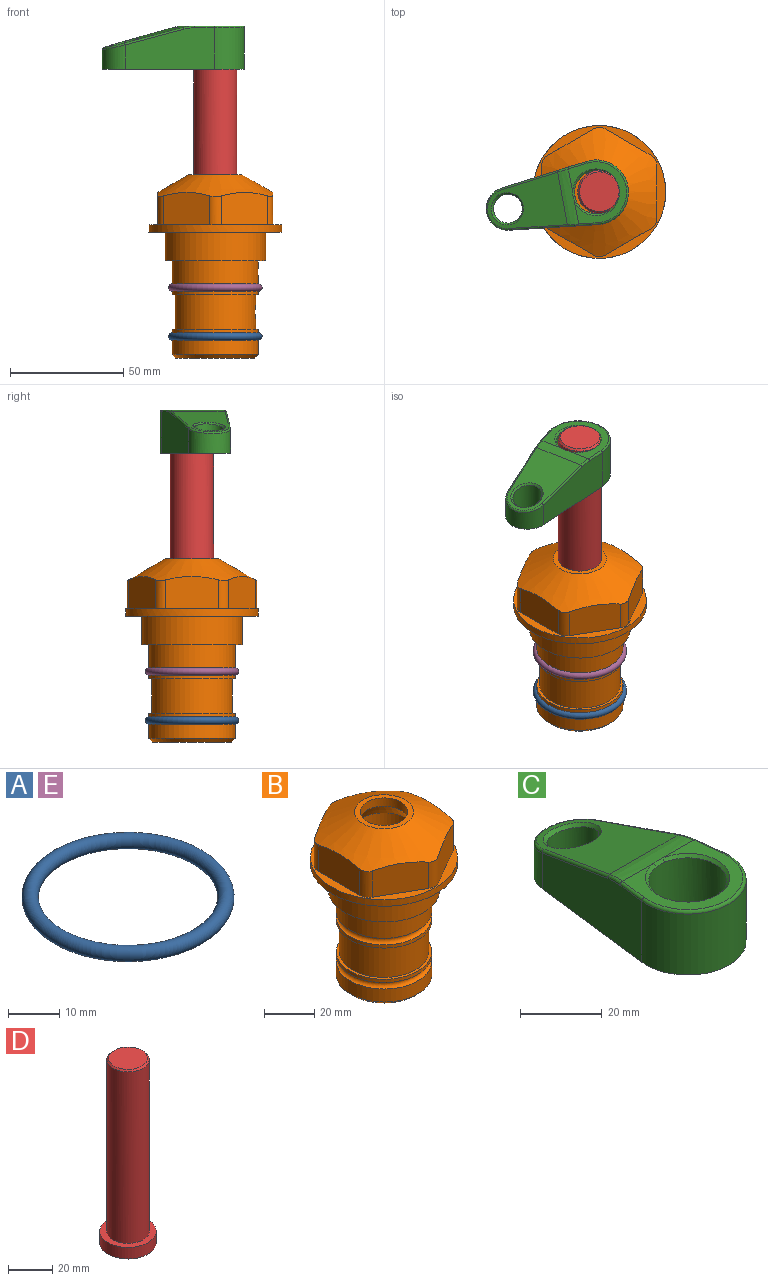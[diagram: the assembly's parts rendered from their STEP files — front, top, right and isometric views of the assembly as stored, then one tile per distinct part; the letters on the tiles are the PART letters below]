
ASSEMBLY  parts=5 mates=4
PART A: 1 faces, bbox 44.7x44.7x3.2 mm
  f0: torus R=19.05mm, axis (0,0,1), area 1193.9mm2
PART B: 36 faces, bbox 58.7x58.7x81 mm
  f0: cylinder r=17.78mm len=35.56mm, axis (0,0,1), area 1670.8mm2, adj f23,f24,f31
  f1: cylinder r=19.05mm len=38.1mm, axis (0,0,1), area 1191.9mm2, adj f26,f27,f30
  f2: plane 58.66x58.66mm, normal (0,0,-1), area 1150.6mm2, adj f3,f28
  f3: cylinder r=29.33mm len=58.66mm, axis (0,0,-1), area 585.1mm2, adj f2,f4
  f4: plane 58.66x58.66mm, normal (0,0,1), area 475.9mm2, adj f3,f5,f6,f7,f8,f9,f10,f11
  f5: plane 20.32x14.34mm, normal (-0.5,0.87,0), area 324.4mm2, adj f4,f15,f16,f17
  f6: plane 20.32x14.34mm, normal (0.5,0.87,0), area 324.4mm2, adj f4,f14,f15,f17
  f7: plane 23.48x14.34mm, normal (1,0,0), area 324.4mm2, adj f4,f13,f14,f17
  f8: plane 20.32x14.34mm, normal (0.5,-0.87,0), area 324.4mm2, adj f4,f12,f13,f17
  f9: plane 20.32x14.34mm, normal (-0.5,-0.87,0), area 324.4mm2, adj f4,f11,f12,f17
  f10: plane 23.48x14.34mm, normal (-1,0,0), area 324.4mm2, adj f4,f11,f16,f17
  f11: cylinder r=5.08mm len=12.85mm, axis (0,0,-1), area 67.2mm2, adj f4,f9,f10,f17
  f12: cylinder r=5.08mm len=12.85mm, axis (0,0,-1), area 67.2mm2, adj f4,f8,f9,f17
  f13: cylinder r=5.08mm len=12.85mm, axis (0,0,-1), area 67.2mm2, adj f4,f7,f8,f17
  f14: cylinder r=5.08mm len=12.85mm, axis (0,0,-1), area 67.2mm2, adj f4,f6,f7,f17
  f15: cylinder r=5.08mm len=12.85mm, axis (0,0,-1), area 67.2mm2, adj f4,f5,f6,f17
  f16: cylinder r=5.08mm len=12.85mm, axis (0,0,-1), area 67.2mm2, adj f4,f5,f10,f17
  f17: cone r=11.73mm half-angle=60deg, axis (0,0,-1), area 2071.8mm2, adj f5,f6,f7,f8,f9,f10,f11,f12
  f18: plane 23.46x23.46mm, normal (0,0,1), area 147.4mm2, adj f17,f35
  f19: plane 34.93x34.93mm, normal (0,0,-1), area 958mm2, adj f29
  f20: cylinder r=19.05mm len=38.1mm, axis (0,0,1), area 760.1mm2, adj f21,f29
  f21: torus R=19.05mm, axis (0,0,1), area 565.3mm2, adj f20,f22
  f22: cylinder r=19.05mm len=38.1mm, axis (0,0,1), area 190mm2, adj f21,f23
  f23: plane 38.1x38.1mm, normal (0,0,1), area 146.9mm2, adj f0,f22
  f24: plane 38.1x38.1mm, normal (0,0,-1), area 146.9mm2, adj f0,f25
  f25: cylinder r=19.05mm len=38.1mm, axis (0,0,1), area 190mm2, adj f24,f26
  f26: torus R=19.05mm, axis (0,0,1), area 565.3mm2, adj f1,f25
  f27: plane 44.45x44.45mm, normal (0,0,-1), area 411.7mm2, adj f1,f28
  f28: cylinder r=22.23mm len=44.45mm, axis (0,0,1), area 1773.5mm2, adj f2,f27
  f29: cone r=19.05mm half-angle=45deg, axis (0,0,1), area 257.5mm2, adj f19,f20
  f30: cylinder r=3.17mm len=6.75mm, axis (-1,0,0), area 128mm2, adj f1,f33
  f31: cylinder r=3.17mm len=6.35mm, axis (-1,0,0), area 102.5mm2, adj f0,f33
  f32: plane 25.4x25.4mm, normal (0,0,1), area 506.7mm2, adj f33
  f33: cylinder r=12.7mm len=66.42mm, axis (0,0,-1), area 5236.2mm2, adj f30,f31,f32,f34
  f34: cone r=9.53mm half-angle=30deg, axis (0,0,-1), area 443.4mm2, adj f33,f35
  f35: cylinder r=9.53mm len=19.05mm, axis (0,0,-1), area 240.9mm2, adj f18,f34
PART C: 31 faces, bbox 31.7x65.5x19.8 mm
  f0: plane 39.12x18.26mm, normal (0.99,0.12,0), area 612.2mm2, adj f1,f4,f7,f11,f13,f15
  f1: cylinder r=9.53mm len=18.91mm, axis (0,0,-1), area 296.1mm2, adj f0,f2,f7,f17
  f2: plane 39.12x18.26mm, normal (-0.99,0.12,0), area 612.2mm2, adj f1,f4,f7,f12,f14,f16
  f3: cylinder r=6.35mm len=12.7mm, axis (0,0,-1), area 362.4mm2, adj f7,f18
  f4: cylinder r=14.29mm len=28.58mm, axis (0,0,-1), area 882.2mm2, adj f0,f2,f7,f10
  f5: cylinder r=9.53mm len=19.05mm, axis (0,0,-1), area 1092.6mm2, adj f7,f19,f20
  f6: plane 26.99x23.69mm, normal (0,0,1), area 216.2mm2, adj f9,f10,f11,f12,f19
  f7: plane 63.5x28.58mm, normal (0,0,-1), area 661.8mm2, adj f0,f1,f2,f3,f4,f5,f22,f23
  f8: plane 33.52x23.6mm, normal (0,0.26,0.97), area 486mm2, adj f9,f15,f16,f17,f18
  f9: cylinder r=19.05mm len=24.72mm, axis (1,0,0), area 120.4mm2, adj f6,f8,f13,f14,f20
  f10: torus R=13.49mm, axis (0,0,1), area 59mm2, adj f4,f6,f11,f12
  f11: cylinder r=0.79mm len=8.67mm, axis (0.12,-0.99,0), area 10.8mm2, adj f0,f6,f10,f13
  f12: cylinder r=0.79mm len=8.67mm, axis (0.12,0.99,0), area 10.8mm2, adj f2,f6,f10,f14
  f13: bspline ~4.95x1.42mm, area 6.1mm2, adj f0,f9,f11,f15
  f14: bspline ~4.95x1.42mm, area 6.1mm2, adj f2,f9,f12,f16
  f15: cylinder r=0.79mm len=25.95mm, axis (0.12,-0.96,0.26), area 32.9mm2, adj f0,f8,f13,f17
  f16: cylinder r=0.79mm len=25.95mm, axis (0.12,0.96,-0.26), area 32.9mm2, adj f2,f8,f14,f17
  f17: bspline ~18.91x8.38mm, area 30mm2, adj f1,f8,f15,f16
  f18: bspline ~14.29x14.29mm, area 48.3mm2, adj f3,f8
  f19: cone r=9.53mm half-angle=45deg, axis (0,0,1), area 66.5mm2, adj f5,f6,f20
  f20: bspline ~3.22x0.96mm, area 3.5mm2, adj f5,f9,f19
  f21: plane 2.75x2.72mm, normal (0,0,-1), area 2.9mm2, adj f23,f25,f28
  f22: plane 23.05x15.88mm, normal (-0.99,-0.12,0), area 323.6mm2, adj f7,f25,f26,f27,f28,f29
  f23: plane 23.05x15.88mm, normal (0.99,-0.12,0), area 323.6mm2, adj f7,f21,f25,f27,f28,f30
  f24: cylinder r=9.53mm len=10.69mm, axis (0,0,-1), area 114.7mm2, adj f7,f27,f29,f30
  f25: cylinder r=12.7mm len=20.59mm, axis (0,0,-1), area 381.1mm2, adj f7,f21,f22,f23,f26,f28
  f26: plane 2.75x2.72mm, normal (0,0,-1), area 2.9mm2, adj f22,f25,f28
  f27: plane 19.72x18.37mm, normal (0,-0.26,-0.97), area 291.8mm2, adj f22,f23,f24,f28,f29,f30
  f28: cylinder r=15.88mm len=19.92mm, axis (1,0,0), area 54.8mm2, adj f21,f22,f23,f25,f26,f27
  f29: cylinder r=1.59mm len=11mm, axis (0,0,-1), area 34.7mm2, adj f7,f22,f24,f27
  f30: cylinder r=1.59mm len=11mm, axis (0,0,-1), area 34.7mm2, adj f7,f23,f24,f27
PART D: 6 faces, bbox 25.4x25.4x101.6 mm
  f0: plane 17.46x17.46mm, normal (0,0,1), area 239.5mm2, adj f5
  f1: plane 25.4x25.4mm, normal (0,0,-1), area 506.7mm2, adj f2
  f2: cylinder r=12.7mm len=25.4mm, axis (0,0,1), area 506.7mm2, adj f1,f3
  f3: plane 25.4x25.4mm, normal (0,0,1), area 221.7mm2, adj f2,f4
  f4: cylinder r=9.53mm len=94.46mm, axis (0,0,1), area 5653mm2, adj f3,f5
  f5: cone r=8.73mm half-angle=45deg, axis (0,0,-1), area 64.4mm2, adj f0,f4
PART E: same geometry as A
PLACE A t=(0,0,-21.59)mm
PLACE B at identity fixed
PLACE C rot(axis=(0,0,1),100.5deg) t=(-1.4,-0.26,27.55)mm
PLACE D rot(axis=(0,0,1),100.5deg) t=(0,0,27.55)mm
PLACE E at identity
MATE fastened E.f0 <-> B.f0  axis (0,0,1) through (0,0,-24.51)mm
MATE fastened A.f0 <-> B.f0  axis (0,0,1) through (0,0,-46.1)mm
MATE cylindrical B.f0 <-> D.f2  axis (0,0,1) through (0,0,-50.55)mm
MATE fastened D.f2 <-> C.f6  axis (0,0,1) through (0,0,91.05)mm
